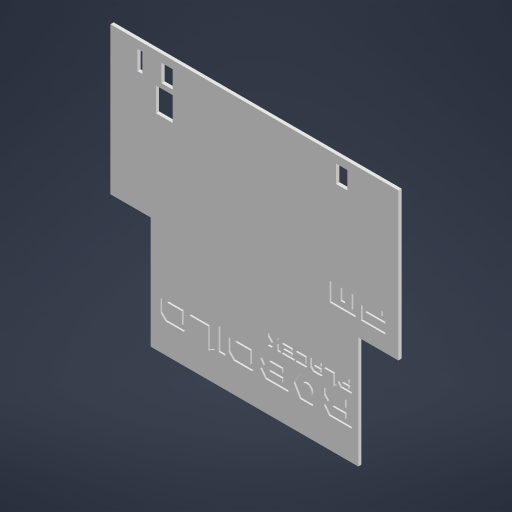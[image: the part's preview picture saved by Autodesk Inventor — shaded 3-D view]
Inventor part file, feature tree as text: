
AUTODESK INVENTOR PART (.ipt)
format: ipt  version: 2023 (Build 270158000, 158)  size: 414,720 bytes
history: native  units: mm
features: reference x15, other x10, extrude x5, sketch x5
ambient origin geometry x8: Origin, YZ Plane, XZ Plane, XY Plane, X Axis, Y Axis, Z Axis, Center Point
bodies: Solid1 (feature_tree)
feature tree (35):
  extrude  "Extrusion1"  Depth=0.2mm
  extrude  "Extrusion2"  Depth=0.2mm
  extrude  "Extrusion3"  Depth=0.2mm
  extrude  "Extrusion4"  Depth=8.0mm
  extrude  "Extrusion5"  Depth=10.0mm
  sketch  "Sketch1"  dims[d0=0.2mm d1=0.2mm]
  reference  "Reference1"
  reference  "Reference2"
  reference  "Reference3"
  reference  "Reference4"
  reference  "Reference5"
  reference  "Reference6"
  sketch  "Sketch2"  dims[d2=0.2mm d3=0.2mm]
  sketch  "Sketch3"  dims[d4=0.2mm d5=0.2mm]
  sketch  "Sketch4"  dims[d6=2.0mm d7=0.0mm]
  sketch  "Sketch5"  dims[d8=15.202mm d9=8.463mm d10=2.639mm d11=12.569mm d12=3.192mm d13=5.694mm d15=3.307mm d17=8.886mm d18=11.062mm d19=2.634mm d20=4.216mm d21=4.216mm d22=1.553mm d23=8.0mm d24=10.0mm d25=29.188762mm d26=121.538877mm d27=16.0mm d28=1.0mm d29=0.0mm d30=1.0mm d31=0.0mm d32=7.0mm d33=1.0mm d34=0.0mm d35=0.0mm d36=0.0mm d37=3.0mm]
  reference  "Reference8"
  reference  "Reference9"
  reference  "Reference10"
  reference  "Reference11"
  reference  "Reference12"
  reference  "Reference15"
  reference  "Reference16"
  reference  "Reference17"
  reference  "Reference18"
  parser-record x1  (decoder bookkeeping rows leaked as tree rows — omitted from the tree; the rows remain in map.json)
  other  "Placek.iam"
  other  "Przod:1"
  other  "tyl:1"
  other  "mocowanie silnika_MIR:1"
  other  "mocowanie silnika:1"
  other  "BokPrawy:1"
  other  "BokPrawy_MIR:1"
  other  "mocowanie-czujniklewy:1"
  other  "mocowanie-czujnika-p:1"
note: 1 file-system path scrubbed to <path> (originals preserved in map.json)
